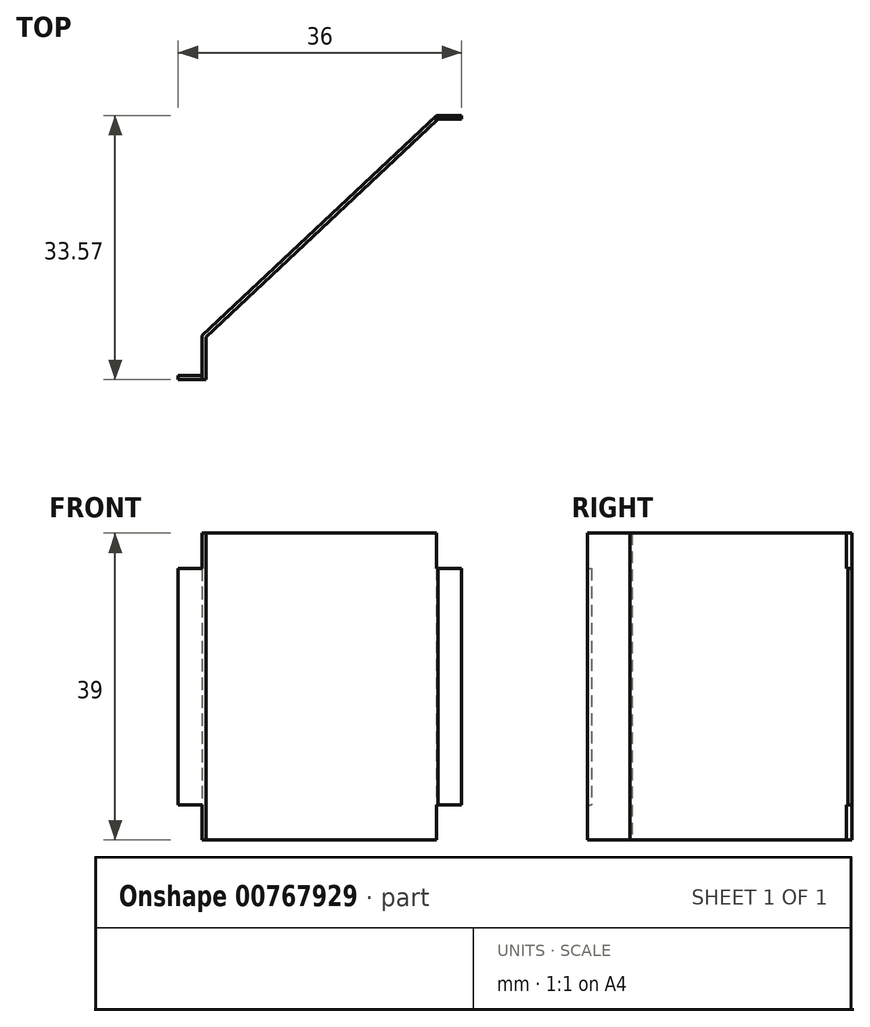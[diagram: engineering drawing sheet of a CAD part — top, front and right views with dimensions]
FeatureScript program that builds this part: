
annotation { "Feature Type Name" : "Feature", "Feature Type Description" : "" }
export const myFeature = defineFeature(function(context is Context, id is Id, definition is map)
    precondition{}
    {
        {
            var Q0;
            Q0=qCreatedBy(makeId("Top.planeOp"),FACE);
            var sketch = newSketch(context, id + "F0", { "sketchPlane" : qUnion([Q0])});
            skLineSegment(sketch, "E0", {"start": v(0.5, 0.6) * mm, "end": v(0.5, 6) * mm});
            skLineSegment(sketch, "E1", {"start": v(0.5, 6) * mm, "end": v(30, 33.67) * mm});
            skLineSegment(sketch, "E2", {"start": v(30, 33.67) * mm, "end": v(33, 33.67) * mm});
            skLineSegment(sketch, "E3.0", {"start": v(29.8, 34.17) * mm, "end": v(33, 34.17) * mm});
            skLineSegment(sketch, "E3.1", {"start": v(0, 6.22) * mm, "end": v(29.8, 34.17) * mm});
            skLineSegment(sketch, "E3.2", {"start": v(0, 1.1) * mm, "end": v(0, 6.22) * mm});
            skLineSegment(sketch, "E4", {"start": v(33, 33.67) * mm, "end": v(33, 34.17) * mm});
            skLineSegment(sketch, "E5", {"start": v(-3, 0.6) * mm, "end": v(-3, 1.1) * mm});
            skLineSegment(sketch, "E6", {"start": v(-3, 1.1) * mm, "end": v(0, 1.1) * mm});
            skLineSegment(sketch, "E7", {"start": v(-3, 0.6) * mm, "end": v(0.5, 0.6) * mm});
            skSolve(sketch);
        }
        {
            var Q0;
            Q0=makeQuery(id+"F0.imprint","IMPRINT",FACE,{"disambiguationData":[TD([[makeQuery(id+"F0.imprint","IMPRINT",EDGE,{"derivedFrom":sQuery(id+"F0.wireOp",EDGE,"E0")}),1.0]])]});
            extrude(context, id + "F1", {"entities" : qUnion([Q0]), "depth" : 39 * mm, "offsetDistance" : 25 * mm});
        }
        {
            var Q0;
            Q0=makeQuery(id+"F1.opExtrude","SWEPT_FACE",FACE,{"disambiguationData":[OSD([sQuery(id+"F0.wireOp",EDGE,"E6")])]});
            var sketch = newSketch(context, id + "F2", { "sketchPlane" : qUnion([Q0])});
            skLineSegment(sketch, "E8.bottom", {"start": v(0, 0) * mm, "end": v(3, 0) * mm});
            skLineSegment(sketch, "E8.top", {"start": v(0, 4.5) * mm, "end": v(3, 4.5) * mm});
            skLineSegment(sketch, "E8.left", {"start": v(0, 0) * mm, "end": v(0, 4.5) * mm});
            skLineSegment(sketch, "E8.right", {"start": v(3, 0) * mm, "end": v(3, 4.5) * mm});
            skLineSegment(sketch, "E9.bottom", {"start": v(3, 39) * mm, "end": v(0, 39) * mm});
            skLineSegment(sketch, "E9.top", {"start": v(3, 34.5) * mm, "end": v(0, 34.5) * mm});
            skLineSegment(sketch, "E9.left", {"start": v(3, 39) * mm, "end": v(3, 34.5) * mm});
            skLineSegment(sketch, "E9.right", {"start": v(0, 39) * mm, "end": v(0, 34.5) * mm});
            skSolve(sketch);
        }
        {
            var Q0;
            Q0 = qSketchRegion(id + "F2", true);
            var Q1;
            Q1=makeQuery(id+"F1.opExtrude","SWEPT_FACE",FACE,{"disambiguationData":[OSD([sQuery(id+"F0.wireOp",EDGE,"E7")])]});
            extrude(context, id + "F3", {"entities" : qUnion([Q0]), "operationType" : NewBodyOperationType.REMOVE, "endBound" : BoundingType.UP_TO_SURFACE, "oppositeDirection" : true, "depth" : 25 * mm, "endBoundEntityFace" : qUnion([Q1]), "offsetDistance" : 25 * mm});
        }
        {
            var Q0;
            Q0=makeQuery(id+"F1.opExtrude","SWEPT_FACE",FACE,{"disambiguationData":[OSD([sQuery(id+"F0.wireOp",EDGE,"E3.0")])]});
            var sketch = newSketch(context, id + "F4", { "sketchPlane" : qUnion([Q0])});
            skLineSegment(sketch, "E10.bottom", {"start": v(-33, 39) * mm, "end": v(-29.8, 39) * mm});
            skLineSegment(sketch, "E10.top", {"start": v(-33, 34.5) * mm, "end": v(-29.8, 34.5) * mm});
            skLineSegment(sketch, "E10.left", {"start": v(-33, 39) * mm, "end": v(-33, 34.5) * mm});
            skLineSegment(sketch, "E10.right", {"start": v(-29.8, 39) * mm, "end": v(-29.8, 34.5) * mm});
            skLineSegment(sketch, "E11.bottom", {"start": v(-33, 0) * mm, "end": v(-29.8, 0) * mm});
            skLineSegment(sketch, "E11.top", {"start": v(-33, 4.5) * mm, "end": v(-29.8, 4.5) * mm});
            skLineSegment(sketch, "E11.left", {"start": v(-33, 0) * mm, "end": v(-33, 4.5) * mm});
            skLineSegment(sketch, "E11.right", {"start": v(-29.8, 0) * mm, "end": v(-29.8, 4.5) * mm});
            skSolve(sketch);
        }
        {
            var Q0;
            Q0 = qSketchRegion(id + "F4", true);
            var Q1;
            Q1=makeQuery(id+"F1.opExtrude","SWEPT_FACE",FACE,{"disambiguationData":[OSD([sQuery(id+"F0.wireOp",EDGE,"E2")])]});
            extrude(context, id + "F5", {"entities" : qUnion([Q0]), "operationType" : NewBodyOperationType.REMOVE, "oppositeDirection" : true, "depth" : 1 * mm, "endBoundEntityFace" : qUnion([Q1]), "offsetDistance" : 25 * mm});
        }
    });
